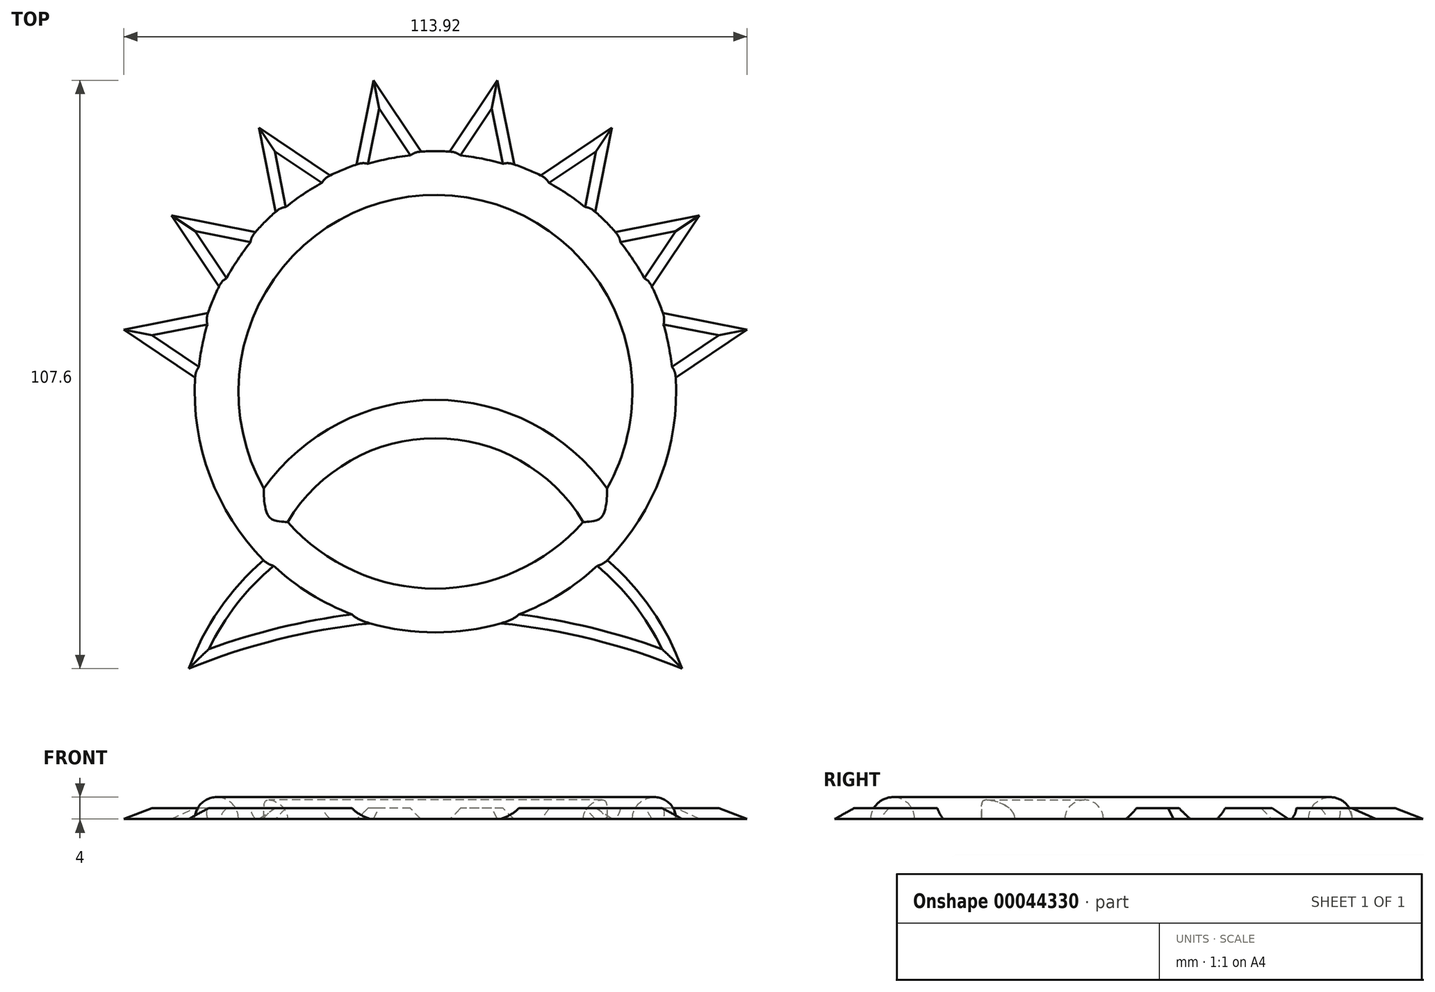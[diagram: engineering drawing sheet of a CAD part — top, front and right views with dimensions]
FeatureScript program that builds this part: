
annotation { "Feature Type Name" : "Feature", "Feature Type Description" : "" }
export const myFeature = defineFeature(function(context is Context, id is Id, definition is map)
    precondition{}
    {
        {
            var Q0;
            Q0=qCreatedBy(makeId("Right.planeOp"),FACE);
            var sketch = newSketch(context, id + "F0", { "sketchPlane" : qUnion([Q0])});
            skCircle(sketch, "E0", {"center": v(-40, 0) * mm, "radius": 4 * mm});
            skLineSegment(sketch, "E1", {"start": v(0, 8.96) * mm, "end": v(0, -14.33) * mm, "construction": true});
            skLineSegment(sketch, "E2", {"start": v(-36, 0) * mm, "end": v(-44, 0) * mm});
            skSolve(sketch);
        }
        {
            var Q0;
            {var subQ0=sQuery(id+"F0.wireOp",EDGE,"E2");Q0=makeQuery(id+"F0.imprint","IMPRINT",FACE,{"disambiguationData":[TD([[makeQuery(id+"F0.imprint","IMPRINT",EDGE,{"derivedFrom":subQ0}),-1.0]])]});}
            var Q1;
            Q1=sQuery(id+"F0.wireOp",EDGE,"E1");
            revolve(context, id + "F1", {"entities" : qUnion([Q0]), "axis" : qUnion([Q1]), "revolveType" : RevolveType.FULL});
        }
        {
            var Q0;
            Q0=qCreatedBy(makeId("Top.planeOp"),FACE);
            var sketch = newSketch(context, id + "F2", { "sketchPlane" : qUnion([Q0])});
            skCircle(sketch, "E3", {"center": v(0, 0) * mm, "radius": 40 * mm, "construction": true});
            skLineSegment(sketch, "E4.0", {"start": v(0, 40) * mm, "end": v(15.3, 36.96) * mm});
            skLineSegment(sketch, "E4.1", {"start": v(15.3, 36.96) * mm, "end": v(28.28, 28.28) * mm});
            skLineSegment(sketch, "E4.2", {"start": v(28.28, 28.28) * mm, "end": v(36.96, 15.3) * mm});
            skLineSegment(sketch, "E4.3", {"start": v(36.96, 15.3) * mm, "end": v(40, 0) * mm});
            skLineSegment(sketch, "E4.4", {"start": v(40, 0) * mm, "end": v(36.96, -15.3) * mm});
            skLineSegment(sketch, "E4.5", {"start": v(36.96, -15.3) * mm, "end": v(28.28, -28.28) * mm});
            skLineSegment(sketch, "E4.6", {"start": v(28.28, -28.28) * mm, "end": v(15.3, -36.96) * mm});
            skLineSegment(sketch, "E4.7", {"start": v(15.3, -36.96) * mm, "end": v(0, -40) * mm});
            skLineSegment(sketch, "E4.8", {"start": v(0, -40) * mm, "end": v(-15.3, -36.96) * mm});
            skLineSegment(sketch, "E4.9", {"start": v(-15.3, -36.96) * mm, "end": v(-28.28, -28.28) * mm});
            skLineSegment(sketch, "E4.10", {"start": v(-28.28, -28.28) * mm, "end": v(-36.96, -15.3) * mm});
            skLineSegment(sketch, "E4.11", {"start": v(-36.96, -15.3) * mm, "end": v(-40, 0) * mm});
            skLineSegment(sketch, "E4.12", {"start": v(-40, 0) * mm, "end": v(-36.96, 15.3) * mm});
            skLineSegment(sketch, "E4.13", {"start": v(-36.96, 15.3) * mm, "end": v(-28.28, 28.28) * mm});
            skLineSegment(sketch, "E4.14", {"start": v(-28.28, 28.28) * mm, "end": v(-15.3, 36.96) * mm});
            skLineSegment(sketch, "E4.15", {"start": v(-15.3, 36.96) * mm, "end": v(0, 40) * mm});
            skLineSegment(sketch, "E5", {"start": v(-40, 0) * mm, "end": v(-56.96, 11.33) * mm});
            skLineSegment(sketch, "E6", {"start": v(-56.96, 11.33) * mm, "end": v(-36.96, 15.3) * mm});
            skLineSegment(sketch, "E7", {"start": v(-36.96, 15.3) * mm, "end": v(-48.28, 32.26) * mm});
            skLineSegment(sketch, "E8", {"start": v(-48.28, 32.26) * mm, "end": v(-28.28, 28.28) * mm});
            skLineSegment(sketch, "E9", {"start": v(-28.28, 28.28) * mm, "end": v(-32.26, 48.28) * mm});
            skLineSegment(sketch, "E10", {"start": v(-32.26, 48.28) * mm, "end": v(-15.3, 36.96) * mm});
            skLineSegment(sketch, "E11", {"start": v(-15.3, 36.96) * mm, "end": v(-11.33, 56.96) * mm});
            skLineSegment(sketch, "E12", {"start": v(-11.33, 56.96) * mm, "end": v(0, 40) * mm});
            skLineSegment(sketch, "E13.MirrorCS", {"start": v(11.33, 56.96) * mm, "end": v(0, 40) * mm});
            skLineSegment(sketch, "E14.MirrorCS", {"start": v(15.3, 36.96) * mm, "end": v(11.33, 56.96) * mm});
            skLineSegment(sketch, "E15.MirrorCS", {"start": v(32.26, 48.28) * mm, "end": v(15.3, 36.96) * mm});
            skLineSegment(sketch, "E16.MirrorCS", {"start": v(28.28, 28.28) * mm, "end": v(32.26, 48.28) * mm});
            skLineSegment(sketch, "E17.MirrorCS", {"start": v(48.28, 32.26) * mm, "end": v(28.28, 28.28) * mm});
            skLineSegment(sketch, "E18.MirrorCS", {"start": v(36.96, 15.3) * mm, "end": v(48.28, 32.26) * mm});
            skLineSegment(sketch, "E19.MirrorCS", {"start": v(56.96, 11.33) * mm, "end": v(36.96, 15.3) * mm});
            skLineSegment(sketch, "E20.MirrorCS", {"start": v(40, 0) * mm, "end": v(56.96, 11.33) * mm});
            skArc(sketch, "E21", {"start": v(-28.28, -28.28) * mm, "mid": v(-38.35, -38.2) * mm, "end": v(-45.08, -50.64) * mm});
            skArc(sketch, "E22.MirrorCS", {"start": v(28.28, -28.28) * mm, "mid": v(38.35, -38.2) * mm, "end": v(45.08, -50.64) * mm});
            skArc(sketch, "E23", {"start": v(45.08, -50.64) * mm, "mid": v(0, -41.74) * mm, "end": v(-45.08, -50.64) * mm});
            skSolve(sketch);
        }
        {
            var Q0;
            Q0=makeQuery(id+"F2.imprint","IMPRINT",FACE,{"disambiguationData":[TD([[makeQuery(id+"F2.imprint","IMPRINT",EDGE,{"derivedFrom":sQuery(id+"F2.wireOp",EDGE,"E4.12")}),1.0]])]});
            var Q1;
            Q1=makeQuery(id+"F2.imprint","IMPRINT",FACE,{"disambiguationData":[TD([[makeQuery(id+"F2.imprint","IMPRINT",EDGE,{"derivedFrom":sQuery(id+"F2.wireOp",EDGE,"E4.13")}),1.0]])]});
            var Q2;
            Q2=makeQuery(id+"F2.imprint","IMPRINT",FACE,{"disambiguationData":[TD([[makeQuery(id+"F2.imprint","IMPRINT",EDGE,{"derivedFrom":sQuery(id+"F2.wireOp",EDGE,"E4.14")}),1.0]])]});
            var Q3;
            Q3=makeQuery(id+"F2.imprint","IMPRINT",FACE,{"disambiguationData":[TD([[makeQuery(id+"F2.imprint","IMPRINT",EDGE,{"derivedFrom":sQuery(id+"F2.wireOp",EDGE,"E4.15")}),1.0]])]});
            var Q4;
            Q4=makeQuery(id+"F2.imprint","IMPRINT",FACE,{"disambiguationData":[TD([[makeQuery(id+"F2.imprint","IMPRINT",EDGE,{"derivedFrom":sQuery(id+"F2.wireOp",EDGE,"E4.0")}),1.0]])]});
            var Q5;
            Q5=makeQuery(id+"F2.imprint","IMPRINT",FACE,{"disambiguationData":[TD([[makeQuery(id+"F2.imprint","IMPRINT",EDGE,{"derivedFrom":sQuery(id+"F2.wireOp",EDGE,"E4.1")}),1.0]])]});
            var Q6;
            Q6=makeQuery(id+"F2.imprint","IMPRINT",FACE,{"disambiguationData":[TD([[makeQuery(id+"F2.imprint","IMPRINT",EDGE,{"derivedFrom":sQuery(id+"F2.wireOp",EDGE,"E4.2")}),1.0]])]});
            var Q7;
            Q7=makeQuery(id+"F2.imprint","IMPRINT",FACE,{"disambiguationData":[TD([[makeQuery(id+"F2.imprint","IMPRINT",EDGE,{"derivedFrom":sQuery(id+"F2.wireOp",EDGE,"E4.3")}),1.0]])]});
            var Q8;
            Q8=makeQuery(id+"F2.imprint","IMPRINT",FACE,{"disambiguationData":[TD([[makeQuery(id+"F2.imprint","IMPRINT",EDGE,{"derivedFrom":sQuery(id+"F2.wireOp",EDGE,"E4.9")}),1.0]])]});
            var Q9;
            Q9=makeQuery(id+"F2.imprint","IMPRINT",FACE,{"disambiguationData":[TD([[makeQuery(id+"F2.imprint","IMPRINT",EDGE,{"derivedFrom":sQuery(id+"F2.wireOp",EDGE,"E4.6")}),1.0]])]});
            extrude(context, id + "F3", {"entities" : qUnion([Q0, Q1, Q2, Q3, Q4, Q5, Q6, Q7, Q8, Q9]), "operationType" : NewBodyOperationType.ADD, "depth" : 2 * mm});
        }
        {
            var Q0;
            Q0=makeQuery(id+"F3.opExtrude","CAP_EDGE",EDGE,{"disambiguationData":[OSD([sQuery(id+"F2.wireOp",EDGE,"E5")])],"isStart":false});
            var Q1;
            Q1=makeQuery(id+"F3.opExtrude","CAP_EDGE",EDGE,{"disambiguationData":[OSD([sQuery(id+"F2.wireOp",EDGE,"E6")])],"isStart":false});
            var Q2;
            Q2=makeQuery(id+"F3.opExtrude","CAP_EDGE",EDGE,{"disambiguationData":[OSD([sQuery(id+"F2.wireOp",EDGE,"E8")])],"isStart":false});
            var Q3;
            Q3=makeQuery(id+"F3.opExtrude","CAP_EDGE",EDGE,{"disambiguationData":[OSD([sQuery(id+"F2.wireOp",EDGE,"E7")])],"isStart":false});
            var Q4;
            Q4=makeQuery(id+"F3.opExtrude","CAP_EDGE",EDGE,{"disambiguationData":[OSD([sQuery(id+"F2.wireOp",EDGE,"E10")])],"isStart":false});
            var Q5;
            Q5=makeQuery(id+"F3.opExtrude","CAP_EDGE",EDGE,{"disambiguationData":[OSD([sQuery(id+"F2.wireOp",EDGE,"E9")])],"isStart":false});
            var Q6;
            Q6=makeQuery(id+"F3.opExtrude","CAP_EDGE",EDGE,{"disambiguationData":[OSD([sQuery(id+"F2.wireOp",EDGE,"E12")])],"isStart":false});
            var Q7;
            Q7=makeQuery(id+"F3.opExtrude","CAP_EDGE",EDGE,{"disambiguationData":[OSD([sQuery(id+"F2.wireOp",EDGE,"E11")])],"isStart":false});
            var Q8;
            Q8=makeQuery(id+"F3.opExtrude","CAP_EDGE",EDGE,{"disambiguationData":[OSD([sQuery(id+"F2.wireOp",EDGE,"E14.MirrorCS")])],"isStart":false});
            var Q9;
            Q9=makeQuery(id+"F3.opExtrude","CAP_EDGE",EDGE,{"disambiguationData":[OSD([sQuery(id+"F2.wireOp",EDGE,"E13.MirrorCS")])],"isStart":false});
            var Q10;
            Q10=makeQuery(id+"F3.opExtrude","CAP_EDGE",EDGE,{"disambiguationData":[OSD([sQuery(id+"F2.wireOp",EDGE,"E16.MirrorCS")])],"isStart":false});
            var Q11;
            Q11=makeQuery(id+"F3.opExtrude","CAP_EDGE",EDGE,{"disambiguationData":[OSD([sQuery(id+"F2.wireOp",EDGE,"E15.MirrorCS")])],"isStart":false});
            var Q12;
            Q12=makeQuery(id+"F3.opExtrude","CAP_EDGE",EDGE,{"disambiguationData":[OSD([sQuery(id+"F2.wireOp",EDGE,"E18.MirrorCS")])],"isStart":false});
            var Q13;
            Q13=makeQuery(id+"F3.opExtrude","CAP_EDGE",EDGE,{"disambiguationData":[OSD([sQuery(id+"F2.wireOp",EDGE,"E17.MirrorCS")])],"isStart":false});
            var Q14;
            Q14=makeQuery(id+"F3.opExtrude","CAP_EDGE",EDGE,{"disambiguationData":[OSD([sQuery(id+"F2.wireOp",EDGE,"E20.MirrorCS")])],"isStart":false});
            var Q15;
            Q15=makeQuery(id+"F3.opExtrude","CAP_EDGE",EDGE,{"disambiguationData":[OSD([sQuery(id+"F2.wireOp",EDGE,"E19.MirrorCS")])],"isStart":false});
            var Q16;
            Q16=makeQuery(id+"F3.opExtrude","CAP_EDGE",EDGE,{"disambiguationData":[OSD([sQuery(id+"F2.wireOp",EDGE,"E21")])],"isStart":false});
            var Q17;
            Q17=makeQuery(id+"F3.opExtrude","CAP_EDGE",EDGE,{"disambiguationData":[OSD([sQuery(id+"F2.wireOp",EDGE,"E23")])],"isStart":false});
            var Q18;
            Q18=makeQuery(id+"F3.opExtrude","CAP_EDGE",EDGE,{"disambiguationData":[OSD([sQuery(id+"F2.wireOp",EDGE,"E22.MirrorCS")])],"isStart":false});
            chamfer(context, id + "F4", {"entities" : qUnion([Q0, Q1, Q2, Q3, Q4, Q5, Q6, Q7, Q8, Q9, Q10, Q11, Q12, Q13, Q14, Q15, Q16, Q17, Q18]), "width" : 2 * mm, "tangentPropagation" : true});
        }
        {
            var Q0;
            Q0=qCreatedBy(makeId("Right.planeOp"),FACE);
            var sketch = newSketch(context, id + "F5", { "sketchPlane" : qUnion([Q0])});
            skLineSegment(sketch, "E24", {"start": v(0, 0) * mm, "end": v(-5, 0) * mm, "construction": true});
            skCircle(sketch, "E25", {"center": v(-5, 0) * mm, "radius": 3.5 * mm});
            skLineSegment(sketch, "E26", {"start": v(-8.5, 0) * mm, "end": v(-1.5, 0) * mm});
            skLineSegment(sketch, "E27", {"start": v(-5, 0) * mm, "end": v(-40, 0) * mm, "construction": true});
            skLineSegment(sketch, "E28", {"start": v(-40, 0) * mm, "end": v(-40, 5.2) * mm, "construction": true});
            skSolve(sketch);
        }
        {
            var Q0;
            {var subQ0=sQuery(id+"F5.wireOp",EDGE,"E26");Q0=makeQuery(id+"F5.imprint","IMPRINT",FACE,{"disambiguationData":[TD([[makeQuery(id+"F5.imprint","IMPRINT",EDGE,{"derivedFrom":subQ0}),1.0]])]});}
            var Q1;
            Q1=sQuery(id+"F5.wireOp",EDGE,"E28");
            revolve(context, id + "F6", {"operationType" : NewBodyOperationType.ADD, "entities" : qUnion([Q0]), "axis" : qUnion([Q1]), "revolveType" : RevolveType.TWO_DIRECTIONS, "angle" : 65 * degree, "angleBack" : 295 * degree});
        }
    });
